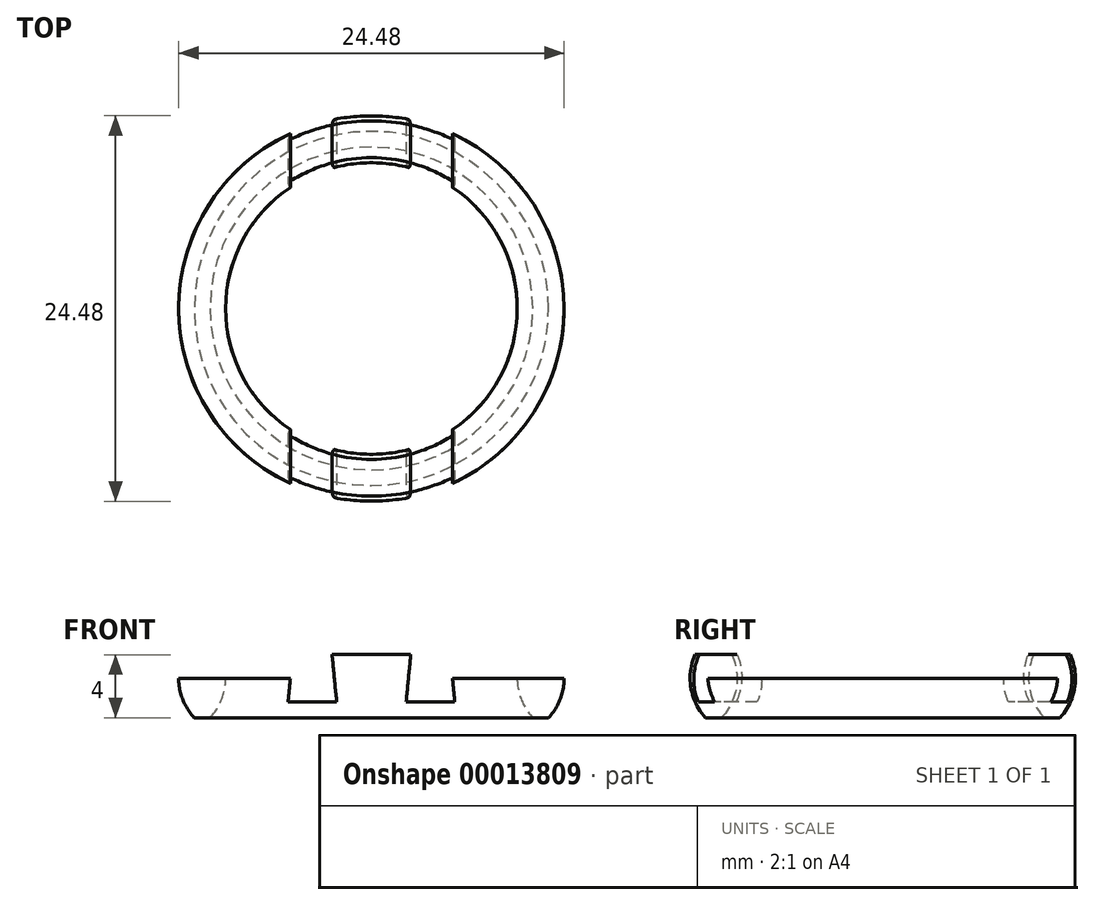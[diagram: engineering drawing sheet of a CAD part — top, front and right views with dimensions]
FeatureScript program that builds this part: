
annotation { "Feature Type Name" : "Feature", "Feature Type Description" : "" }
export const myFeature = defineFeature(function(context is Context, id is Id, definition is map)
    precondition{}
    {
        {
            var Q0;
            Q0=qCreatedBy(makeId("Front.planeOp"),FACE);
            var sketch = newSketch(context, id + "F0", { "sketchPlane" : qUnion([Q0])});
            skLineSegment(sketch, "E0", {"start": v(0, 0) * mm, "end": v(0, 5) * mm});
            skArc(sketch, "E1", {"start": v(-10.25, 0) * mm, "mid": v(-9.26, 2.5) * mm, "end": v(-10.25, 5) * mm});
            skLineSegment(sketch, "E2", {"start": v(-11.25, 5) * mm, "end": v(-10.25, 5) * mm});
            skLineSegment(sketch, "E3", {"start": v(-11.25, 0) * mm, "end": v(-10.25, 0) * mm});
            skArc(sketch, "E4", {"start": v(-11.25, 5) * mm, "mid": v(-12.24, 2.5) * mm, "end": v(-11.25, 0) * mm});
            skPoint(sketch, "E5.orphan", {"position": v(-12.25, 5) * mm});
            skPoint(sketch, "E6.orphan", {"position": v(-12.25, 0) * mm});
            skSolve(sketch);
        }
        {
            var Q0;
            Q0 = qSketchRegion(id + "F0", true);
            var Q1;
            Q1=sQuery(id+"F0.wireOp",EDGE,"E0");
            revolve(context, id + "F1", {"entities" : qUnion([Q0]), "axis" : qUnion([Q1]), "revolveType" : RevolveType.FULL});
        }
        {
            var Q0;
            Q0=qCreatedBy(makeId("Front.planeOp"),FACE);
            var sketch = newSketch(context, id + "F2", { "sketchPlane" : qUnion([Q0])});
            skLineSegment(sketch, "E7", {"start": v(-12.26, 2.5) * mm, "end": v(-5.15, 2.5) * mm});
            skLineSegment(sketch, "E8", {"start": v(-12.26, 2.5) * mm, "end": v(-12.26, 5.63) * mm});
            skLineSegment(sketch, "E9", {"start": v(0, 0) * mm, "end": v(0, 4.5) * mm});
            skLineSegment(sketch, "E10", {"start": v(0, 2.5) * mm, "end": v(0, 3.83) * mm});
            skLineSegment(sketch, "E11", {"start": v(0, 2.5) * mm, "end": v(0, 3.47) * mm});
            skLineSegment(sketch, "E12", {"start": v(0, 2.5) * mm, "end": v(0, 4.5) * mm});
            skLineSegment(sketch, "E13", {"start": v(-2.5, 4) * mm, "end": v(-2.2, 1) * mm});
            skLineSegment(sketch, "E14.0", {"start": v(-5.3, 1) * mm, "end": v(-2.2, 1) * mm});
            skLineSegment(sketch, "E15.0.MirrorCS", {"start": v(-5.15, 2.5) * mm, "end": v(-5.3, 1) * mm});
            skLineSegment(sketch, "E16.trimOffspring", {"start": v(-2.5, 4) * mm, "end": v(0, 4) * mm});
            skLineSegment(sketch, "E17.0.MirrorCS", {"start": v(12.26, 2.5) * mm, "end": v(12.26, 5.63) * mm});
            skLineSegment(sketch, "E18.0.MirrorCS", {"start": v(12.26, 2.5) * mm, "end": v(5.15, 2.5) * mm});
            skLineSegment(sketch, "E19.0.MirrorCS", {"start": v(5.15, 2.5) * mm, "end": v(5.3, 1) * mm});
            skLineSegment(sketch, "E20.0.MirrorCS", {"start": v(5.3, 1) * mm, "end": v(2.2, 1) * mm});
            skLineSegment(sketch, "E21.0.MirrorCS", {"start": v(2.5, 4) * mm, "end": v(2.2, 1) * mm});
            skLineSegment(sketch, "E22.0.MirrorCS", {"start": v(2.5, 4) * mm, "end": v(0, 4) * mm});
            skLineSegment(sketch, "E23", {"start": v(-12.26, 5.63) * mm, "end": v(12.26, 5.63) * mm});
            skLineSegment(sketch, "E24.trimOffspring", {"start": v(0, 5.63) * mm, "end": v(0, 5.9) * mm});
            skPoint(sketch, "E25.0.MirrorCS.end.orphan", {"position": v(6.1, 2.5) * mm});
            skPoint(sketch, "E26.0.MirrorCS.start.orphan", {"position": v(6.25, 4) * mm});
            skPoint(sketch, "E27.orphan", {"position": v(5, 4) * mm});
            skPoint(sketch, "E28.0.MirrorCS.end.orphan", {"position": v(-6.1, 2.5) * mm});
            skPoint(sketch, "E28.0.MirrorCS.start.orphan", {"position": v(-6.25, 4) * mm});
            skPoint(sketch, "E29.orphan", {"position": v(-5, 4) * mm});
            skSolve(sketch);
        }
        {
            var Q0;
            Q0=makeQuery(id+"F2.imprint","IMPRINT",FACE,{"disambiguationData":[TD([[makeQuery(id+"F2.imprint","IMPRINT",EDGE,{"derivedFrom":sQuery(id+"F2.wireOp",EDGE,"E7")}),1.0]])]});
            extrude(context, id + "F3", {"entities" : qUnion([Q0]), "operationType" : NewBodyOperationType.REMOVE, "endBound" : BoundingType.SYMMETRIC, "oppositeDirection" : true, "depth" : 25 * mm});
        }
    });
